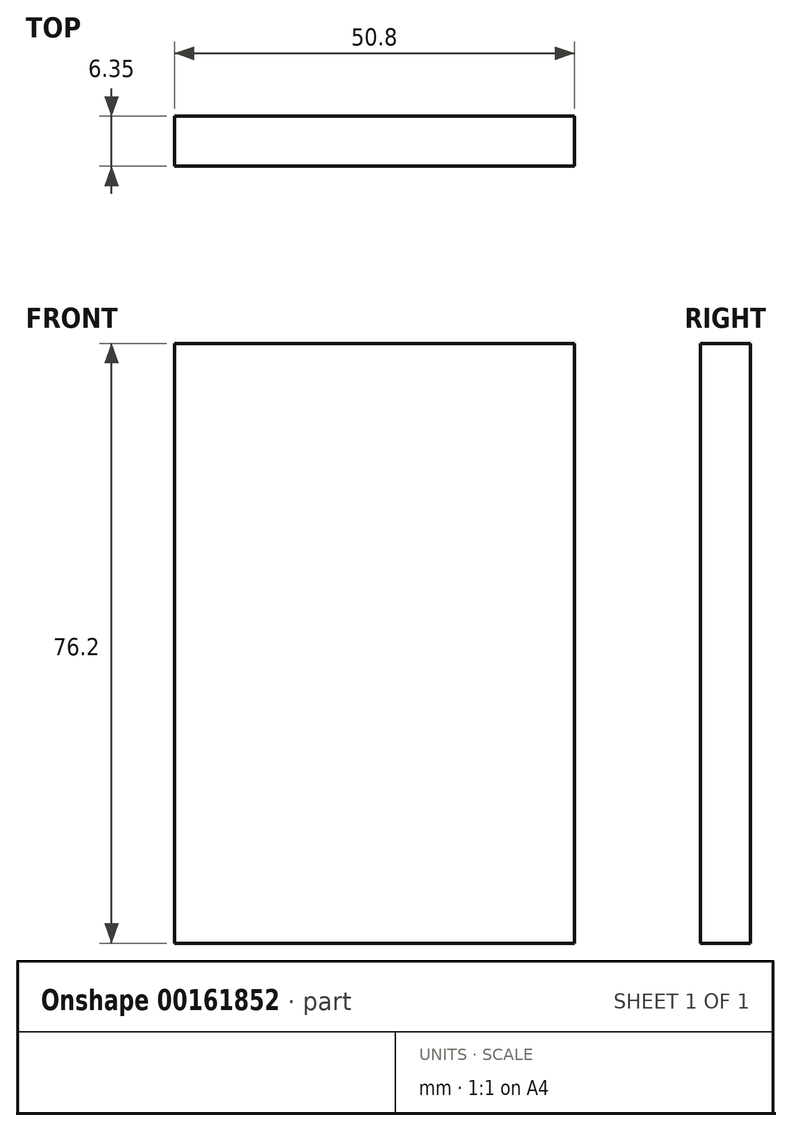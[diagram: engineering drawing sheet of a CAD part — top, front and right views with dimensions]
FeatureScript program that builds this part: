
annotation { "Feature Type Name" : "Feature", "Feature Type Description" : "" }
export const myFeature = defineFeature(function(context is Context, id is Id, definition is map)
    precondition{}
    {
        {
            var Q0;
            Q0=qCreatedBy(makeId("Front.planeOp"),FACE);
            var sketch = newSketch(context, id + "F0", { "sketchPlane" : qUnion([Q0])});
            skLineSegment(sketch, "E0.bottom", {"start": v(-77.98, 41.4) * mm, "end": v(-27.18, 41.4) * mm});
            skLineSegment(sketch, "E0.top", {"start": v(-77.98, -34.8) * mm, "end": v(-27.18, -34.8) * mm});
            skLineSegment(sketch, "E0.left", {"start": v(-77.98, 41.4) * mm, "end": v(-77.98, -34.8) * mm});
            skLineSegment(sketch, "E0.right", {"start": v(-27.18, 41.4) * mm, "end": v(-27.18, -34.8) * mm});
            skSolve(sketch);
        }
        {
            var Q0;
            Q0 = qSketchRegion(id + "F0", true);
            extrude(context, id + "F1", {"entities" : qUnion([Q0]), "depth" : 6.35 * mm});
        }
    });
